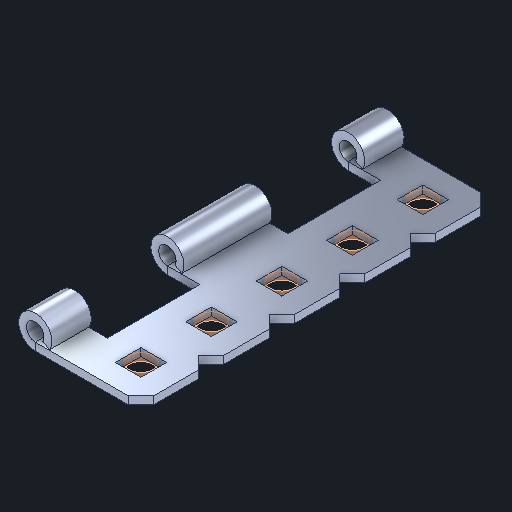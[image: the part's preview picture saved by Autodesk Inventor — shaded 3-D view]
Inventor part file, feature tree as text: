
AUTODESK INVENTOR PART (.ipt)
format: ipt  version: 2024 (Build 280153000, 153)  size: 242,176 bytes
history: native  units: in
note: dims shown in document units (in); Inventor stores cm internally (conversion verified against a paired STEP export)
features: other x14, sketch x1
ambient origin geometry x8: Origin, YZ Plane, XZ Plane, XY Plane, X Axis, Y Axis, Z Axis, Center Point
bodies: Body1 (feature_tree), Body2 (feature_tree), Body3 (feature_tree), Body4 (feature_tree), Body5 (feature_tree), Body6 (feature_tree)
feature tree (15):
  other  "Top 5.ipt"
  other  "Cut-Extrude3::Top 5.ipt"
  other  "TaggingFeature1"
  sketch  "Sketch1"  dims[d0=0.3937in]
  other  "Srf1"
  other  "Srf2"
  other  "Srf3"
  other  "Srf4"
  other  "Srf5"
  other  "Cut-Extrude3"
  other  "Srf1::Derived"
  other  "Srf2::Derived"
  other  "Srf3::Derived"
  other  "Srf4::Derived"
  other  "Srf5::Derived"
